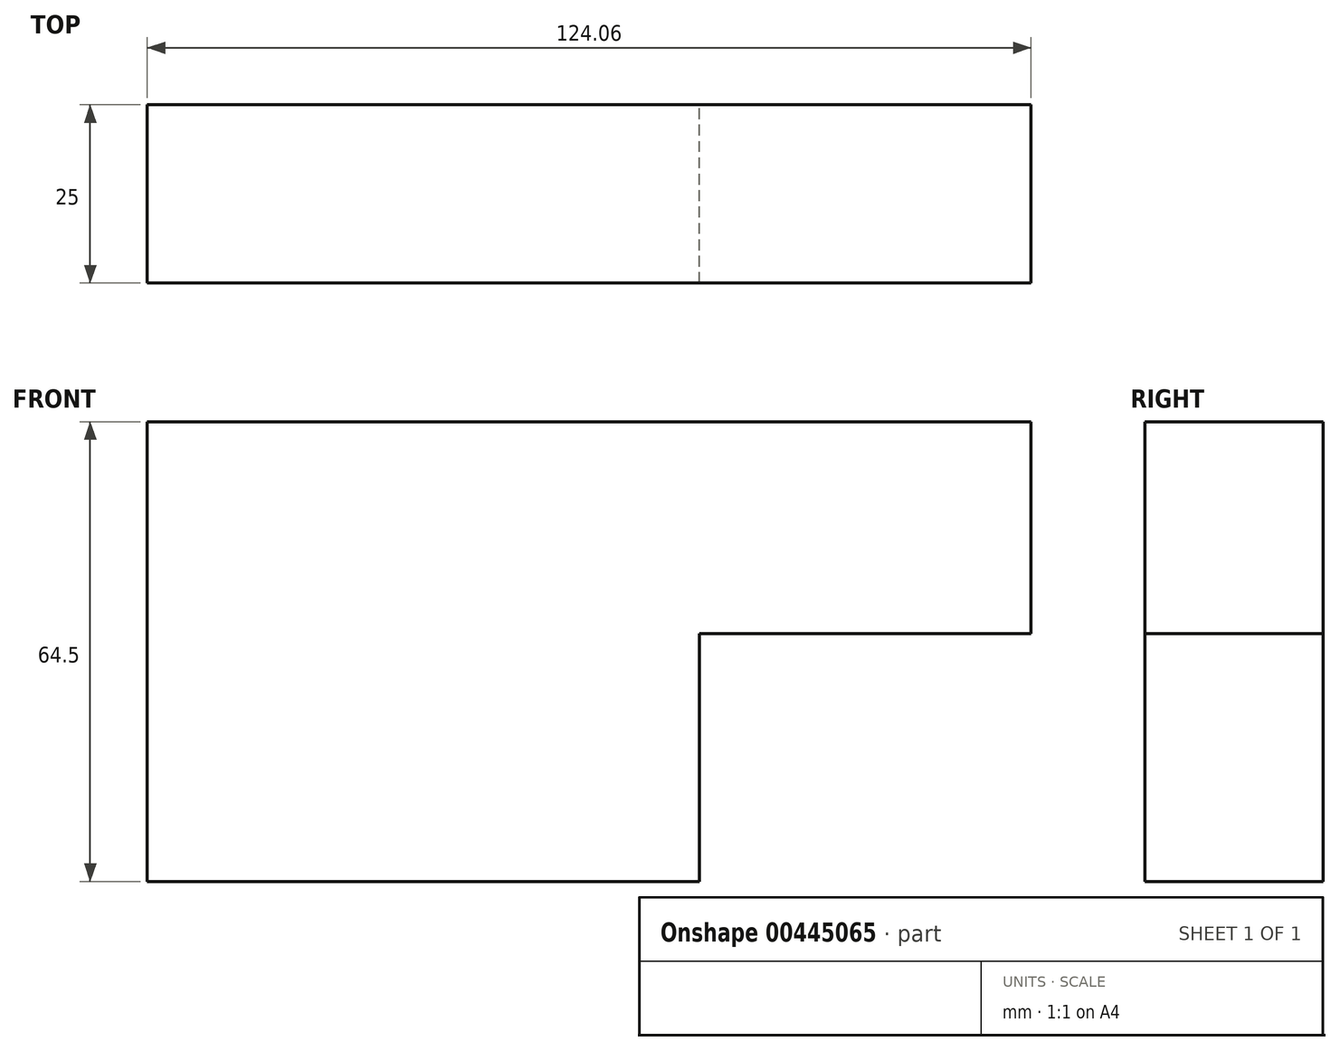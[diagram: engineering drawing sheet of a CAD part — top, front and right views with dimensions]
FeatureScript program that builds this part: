
annotation { "Feature Type Name" : "Feature", "Feature Type Description" : "" }
export const myFeature = defineFeature(function(context is Context, id is Id, definition is map)
    precondition{}
    {
        {
            var Q0;
            Q0=qCreatedBy(makeId("Front.planeOp"),FACE);
            var sketch = newSketch(context, id + "F0", { "sketchPlane" : qUnion([Q0])});
            skLineSegment(sketch, "E0.bottom", {"start": v(-75.4, 50.81) * mm, "end": v(2.14, 50.81) * mm});
            skLineSegment(sketch, "E0.top", {"start": v(-75.4, -13.7) * mm, "end": v(2.14, -13.7) * mm});
            skLineSegment(sketch, "E0.left", {"start": v(-75.4, 50.81) * mm, "end": v(-75.4, -13.7) * mm});
            skLineSegment(sketch, "E0.right", {"start": v(2.14, 21.12) * mm, "end": v(2.14, -13.7) * mm});
            skLineSegment(sketch, "E1.bottom", {"start": v(2.14, 50.81) * mm, "end": v(48.67, 50.81) * mm});
            skLineSegment(sketch, "E1.top", {"start": v(2.14, 21.12) * mm, "end": v(48.67, 21.12) * mm});
            skLineSegment(sketch, "E1.right", {"start": v(48.67, 50.81) * mm, "end": v(48.67, 21.12) * mm});
            skSolve(sketch);
        }
        {
            var Q0;
            Q0=makeQuery(id+"F0.imprint","IMPRINT",FACE,{"disambiguationData":[TD([[makeQuery(id+"F0.imprint","IMPRINT",EDGE,{"derivedFrom":sQuery(id+"F0.wireOp",EDGE,"E0.bottom")}),-1.0]])]});
            var Q1;
            Q1 = qSketchRegion(id + "F0", true);
            extrude(context, id + "F1", {"entities" : qUnion([Q0, Q1]), "depth" : 25 * mm});
        }
    });
